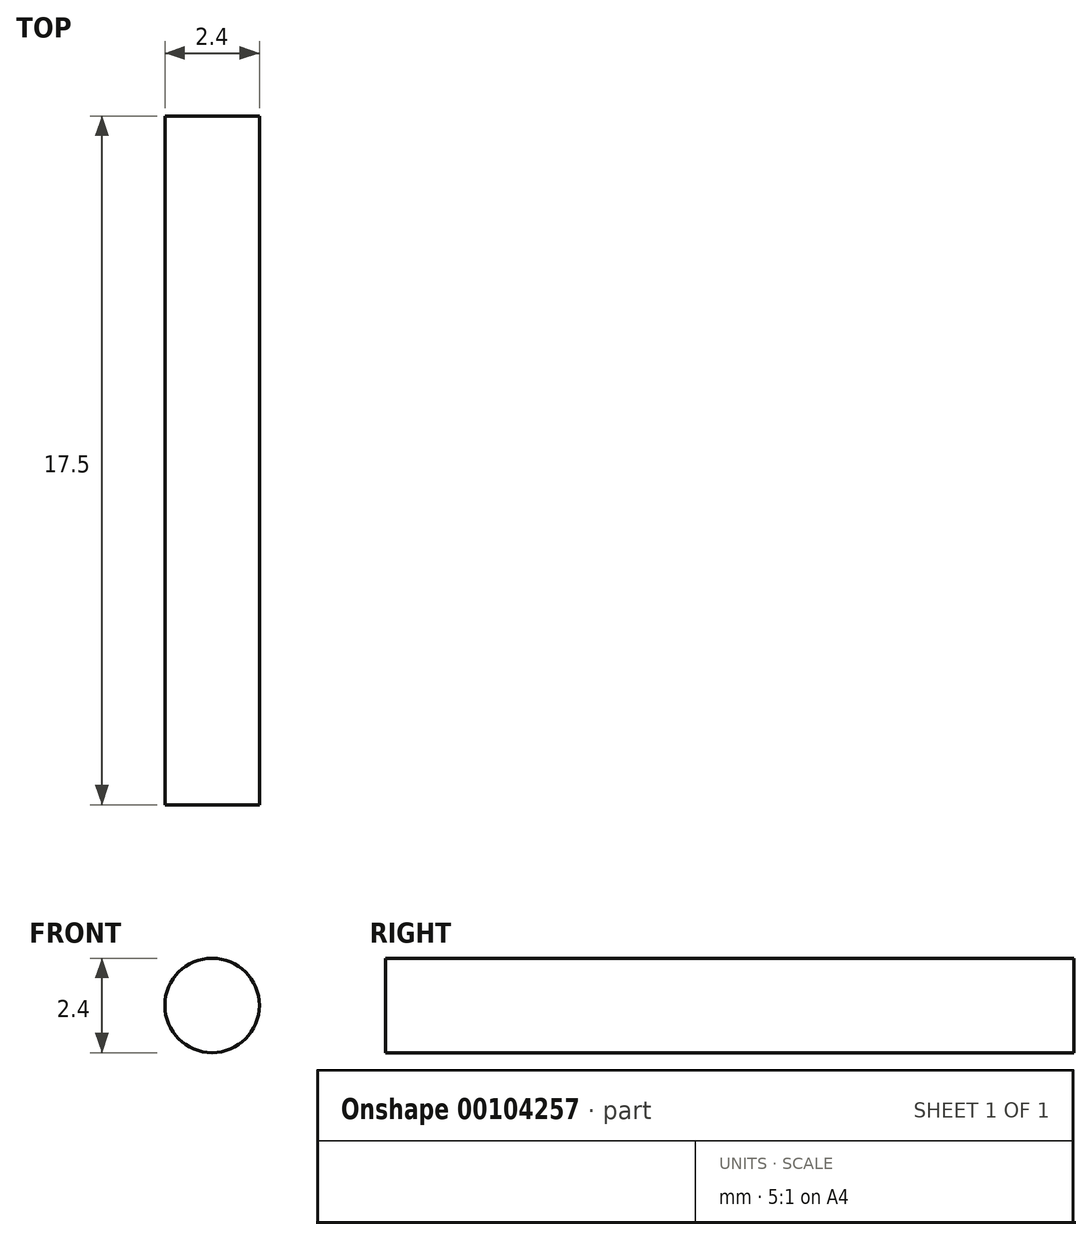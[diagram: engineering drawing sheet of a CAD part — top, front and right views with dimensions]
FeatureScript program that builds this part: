
annotation { "Feature Type Name" : "Feature", "Feature Type Description" : "" }
export const myFeature = defineFeature(function(context is Context, id is Id, definition is map)
    precondition{}
    {
        {
            var Q0;
            Q0=qCreatedBy(makeId("Front.planeOp"),FACE);
            var sketch = newSketch(context, id + "F0", { "sketchPlane" : qUnion([Q0])});
            skCircle(sketch, "E0", {"center": v(0, 0) * mm, "radius": 1.2 * mm});
            skSolve(sketch);
        }
        {
            var Q0;
            Q0 = qSketchRegion(id + "F0", true);
            extrude(context, id + "F1", {"entities" : qUnion([Q0]), "depth" : 17.5 * mm});
        }
    });
